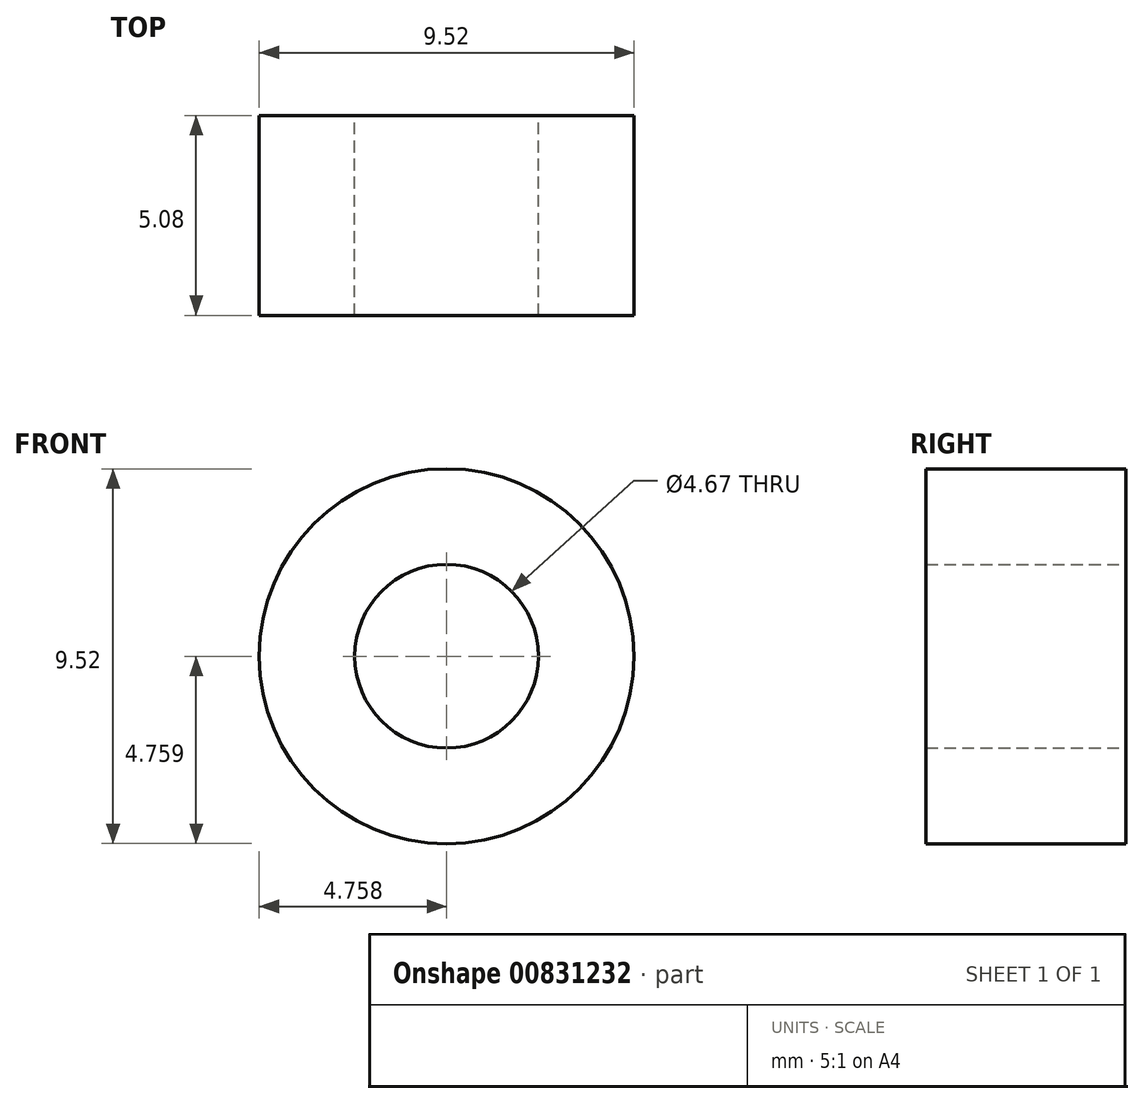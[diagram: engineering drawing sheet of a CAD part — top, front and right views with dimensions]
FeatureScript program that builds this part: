
annotation { "Feature Type Name" : "Feature", "Feature Type Description" : "" }
export const myFeature = defineFeature(function(context is Context, id is Id, definition is map)
    precondition{}
    {
        {
            var Q0;
            Q0=qCreatedBy(makeId("Front.planeOp"),FACE);
            var sketch = newSketch(context, id + "F0", { "sketchPlane" : qUnion([Q0])});
            skCircle(sketch, "E0", {"center": v(-62.1, 45.63) * mm, "radius": 4.76 * mm});
            skCircle(sketch, "E1", {"center": v(-62.1, 45.63) * mm, "radius": 2.33 * mm});
            skSolve(sketch);
        }
        {
            var Q0;
            Q0=makeQuery(id+"F0.imprint","IMPRINT",FACE,{"disambiguationData":[TD([[makeQuery(id+"F0.imprint","IMPRINT",EDGE,{"derivedFrom":sQuery(id+"F0.wireOp",EDGE,"E0")}),1.0]])]});
            extrude(context, id + "F1", {"entities" : qUnion([Q0]), "depth" : 5.08 * mm, "offsetDistance" : 25.4 * mm});
        }
    });
